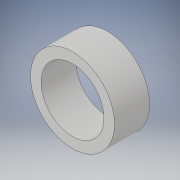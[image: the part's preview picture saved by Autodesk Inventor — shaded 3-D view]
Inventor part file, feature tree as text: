
AUTODESK INVENTOR PART (.ipt)
format: ipt  version: 2019 (Build 230136000, 136)  size: 102,400 bytes
history: native  units: mm
features: extrude x2, sketch x2
ambient origin geometry x8: Origin, YZ Plane, XZ Plane, XY Plane, X Axis, Y Axis, Z Axis, Center Point
bodies: Solid1 (feature_tree)
feature tree (4):
  extrude  "Extrusion1"  Depth=10.0mm TaperAngle=0.0deg
  extrude  "Extrusion2"  Depth=10.0mm TaperAngle=0.0deg
  sketch  "Sketch1"  dims[d0=24.0mm d1=10.0mm d2=0.0mm]
  sketch  "Sketch2"  dims[d3=18.0mm d4=10.0mm d5=0.0mm]
